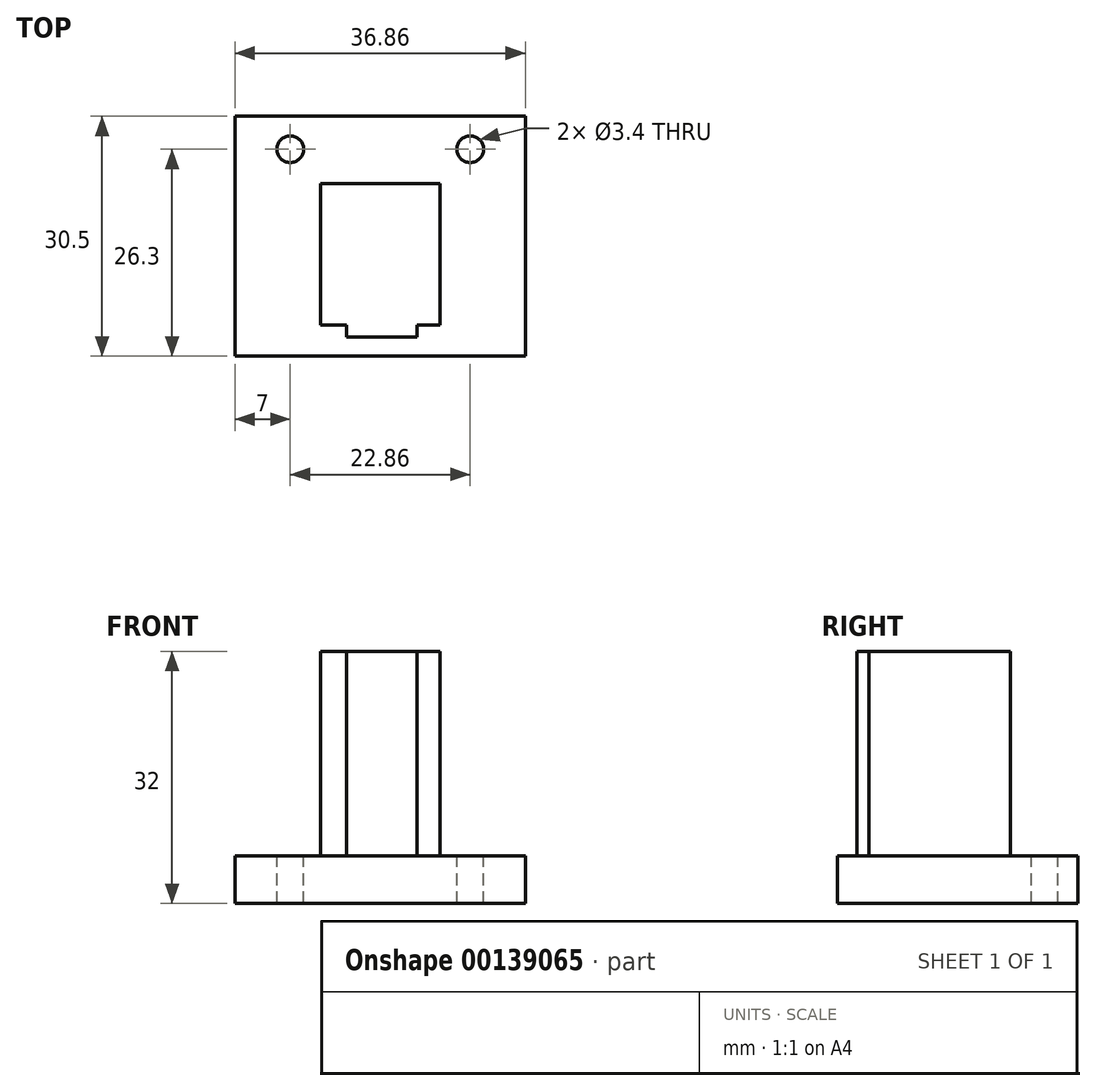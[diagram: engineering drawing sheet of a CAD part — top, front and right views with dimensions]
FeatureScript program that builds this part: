
annotation { "Feature Type Name" : "Feature", "Feature Type Description" : "" }
export const myFeature = defineFeature(function(context is Context, id is Id, definition is map)
    precondition{}
    {
        {
            var Q0;
            Q0=qCreatedBy(makeId("Top.planeOp"),FACE);
            var sketch = newSketch(context, id + "F0", { "sketchPlane" : qUnion([Q0])});
            skLineSegment(sketch, "E0.bottom", {"start": v(18.43, 15.25) * mm, "end": v(-18.43, 15.25) * mm});
            skLineSegment(sketch, "E0.top", {"start": v(18.43, -15.25) * mm, "end": v(-18.43, -15.25) * mm});
            skLineSegment(sketch, "E0.left", {"start": v(18.43, 15.25) * mm, "end": v(18.43, -15.25) * mm});
            skLineSegment(sketch, "E0.right", {"start": v(-18.43, 15.25) * mm, "end": v(-18.43, -15.25) * mm});
            skPoint(sketch, "E0.middle", {"position": v(0, 0) * mm});
            skSolve(sketch);
        }
        {
            var Q0;
            Q0 = qSketchRegion(id + "F0", true);
            extrude(context, id + "F1", {"entities" : qUnion([Q0]), "depth" : 6 * mm});
        }
        {
            var Q0;
            Q0=makeQuery(id+"F1.opExtrude","CAP_FACE",FACE,{"disambiguationData":[OSD([sQuery(id+"F0.wireOp",EDGE,"E0.bottom"),sQuery(id+"F0.wireOp",EDGE,"E0.top"),sQuery(id+"F0.wireOp",EDGE,"E0.left"),sQuery(id+"F0.wireOp",EDGE,"E0.right")])],"isStart":false});
            var sketch = newSketch(context, id + "F2", { "sketchPlane" : qUnion([Q0])});
            skCircle(sketch, "E1", {"center": v(-11.43, 11.05) * mm, "radius": 1.7 * mm});
            skCircle(sketch, "E2", {"center": v(11.43, 11.05) * mm, "radius": 1.7 * mm});
            skSolve(sketch);
        }
        {
            var Q0;
            Q0 = qSketchRegion(id + "F2", true);
            extrude(context, id + "F3", {"entities" : qUnion([Q0]), "operationType" : NewBodyOperationType.REMOVE, "oppositeDirection" : true, "depth" : 25 * mm});
        }
        {
            var Q0;
            Q0=makeQuery(id+"F1.opExtrude","CAP_FACE",FACE,{"disambiguationData":[OSD([sQuery(id+"F0.wireOp",EDGE,"E0.bottom"),sQuery(id+"F0.wireOp",EDGE,"E0.top"),sQuery(id+"F0.wireOp",EDGE,"E0.left"),sQuery(id+"F0.wireOp",EDGE,"E0.right")])],"isStart":false});
            var sketch = newSketch(context, id + "F4", { "sketchPlane" : qUnion([Q0])});
            skLineSegment(sketch, "E3.bottom", {"start": v(-7.6, -11.3) * mm, "end": v(7.61, -11.3) * mm});
            skLineSegment(sketch, "E3.top", {"start": v(-7.6, 6.7) * mm, "end": v(7.61, 6.7) * mm});
            skLineSegment(sketch, "E3.left", {"start": v(-7.6, -11.3) * mm, "end": v(-7.6, 6.7) * mm});
            skLineSegment(sketch, "E3.right", {"start": v(7.61, -11.3) * mm, "end": v(7.61, 6.7) * mm});
            skLineSegment(sketch, "E4.bottom", {"start": v(-4.26, -11.3) * mm, "end": v(4.65, -11.3) * mm});
            skLineSegment(sketch, "E4.top", {"start": v(-4.26, -12.8) * mm, "end": v(4.65, -12.8) * mm});
            skLineSegment(sketch, "E4.left", {"start": v(-4.26, -11.3) * mm, "end": v(-4.26, -12.8) * mm});
            skLineSegment(sketch, "E4.right", {"start": v(4.65, -11.3) * mm, "end": v(4.65, -12.8) * mm});
            skSolve(sketch);
        }
        {
            var Q0;
            Q0 = qSketchRegion(id + "F4", true);
            extrude(context, id + "F5", {"entities" : qUnion([Q0]), "operationType" : NewBodyOperationType.ADD, "depth" : 26 * mm});
        }
    });
